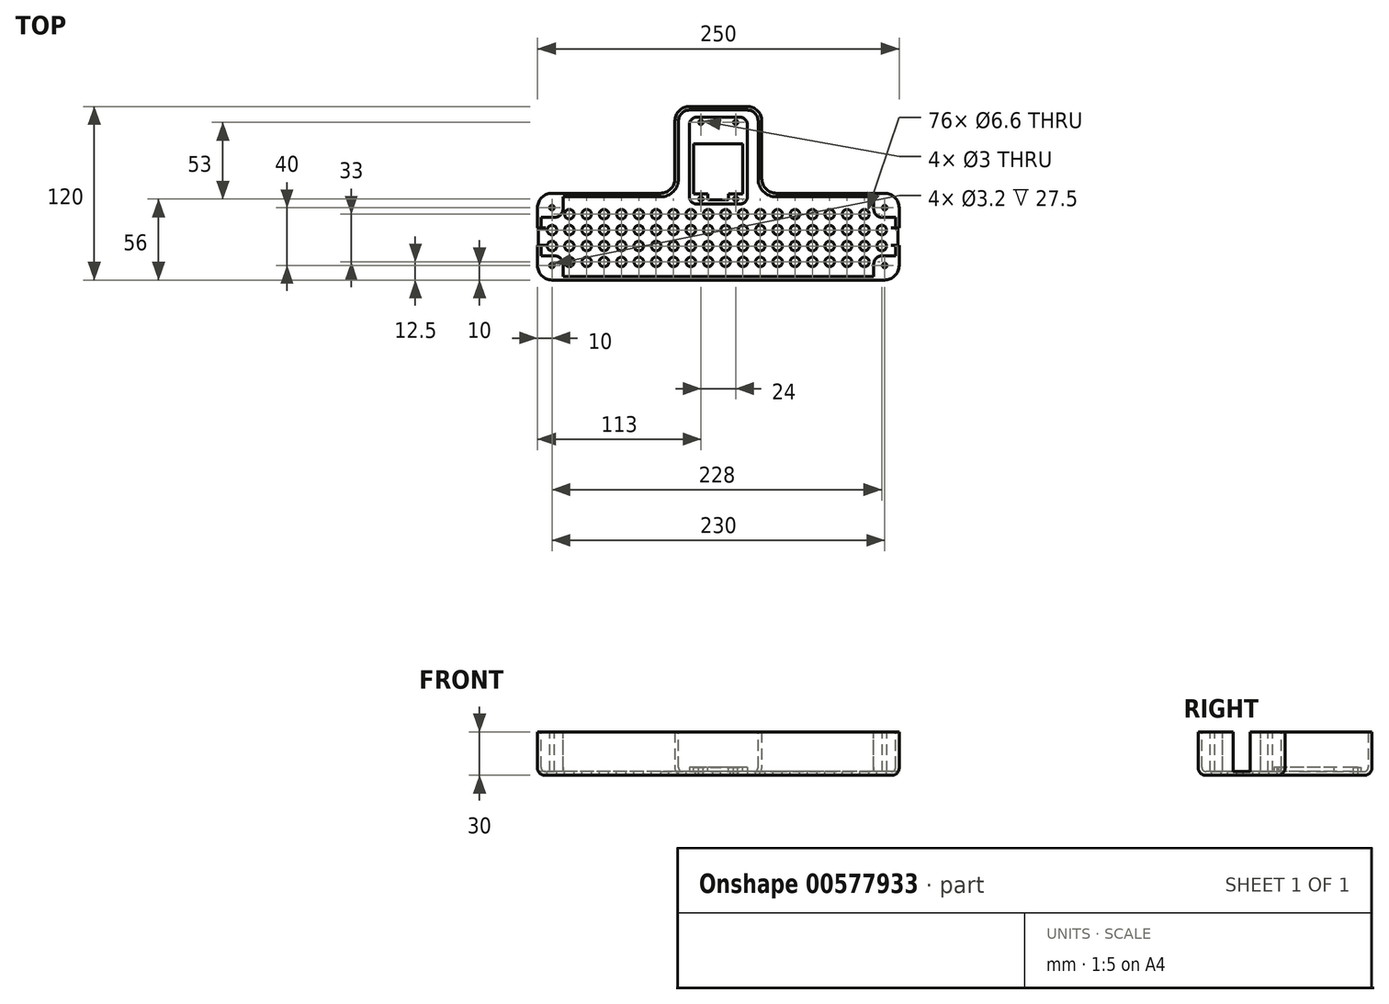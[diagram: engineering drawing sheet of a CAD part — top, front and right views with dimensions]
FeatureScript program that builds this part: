
annotation { "Feature Type Name" : "Feature", "Feature Type Description" : "" }
export const myFeature = defineFeature(function(context is Context, id is Id, definition is map)
    precondition{}
    {
        {
            var Q0;
            Q0=qCreatedBy(makeId("Top.planeOp"),FACE);
            var sketch = newSketch(context, id + "F0", { "sketchPlane" : qUnion([Q0])});
            skLineSegment(sketch, "E0.top", {"start": v(125, -30) * mm, "end": v(-125, -30) * mm});
            skLineSegment(sketch, "E0.left", {"start": v(125, 30) * mm, "end": v(125, -30) * mm});
            skLineSegment(sketch, "E0.right", {"start": v(-125, 30) * mm, "end": v(-125, -30) * mm});
            skPoint(sketch, "E0.middle", {"position": v(0, 0) * mm});
            skLineSegment(sketch, "E1.top", {"start": v(30, 90) * mm, "end": v(-30, 90) * mm});
            skLineSegment(sketch, "E1.left", {"start": v(30, 30) * mm, "end": v(30, 90) * mm});
            skLineSegment(sketch, "E1.right", {"start": v(-30, 30) * mm, "end": v(-30, 90) * mm});
            skLineSegment(sketch, "E2.trimOffspring", {"start": v(-30, 30) * mm, "end": v(-125, 30) * mm});
            skLineSegment(sketch, "E3", {"start": v(30, 30) * mm, "end": v(125, 30) * mm});
            skSolve(sketch);
        }
        {
            var Q0;
            Q0 = qSketchRegion(id + "F0", true);
            extrude(context, id + "F1", {"entities" : qUnion([Q0]), "depth" : 30 * mm, "offsetDistance" : 25 * mm});
        }
        {
            var Q0;
            Q0=makeQuery(id+"F1.opExtrude","SWEPT_EDGE",EDGE,{"disambiguationData":[OSD([sQuery(id+"F0.wireOp",EDGE,"E1.left"),sQuery(id+"F0.wireOp",EDGE,"E3")])]});
            var Q1;
            Q1=makeQuery(id+"F1.opExtrude","SWEPT_EDGE",EDGE,{"disambiguationData":[OSD([sQuery(id+"F0.wireOp",EDGE,"E1.right"),sQuery(id+"F0.wireOp",EDGE,"E2.trimOffspring")])]});
            var Q2;
            Q2=makeQuery(id+"F1.opExtrude","SWEPT_EDGE",EDGE,{"disambiguationData":[OSD([sQuery(id+"F0.wireOp",EDGE,"E1.top"),sQuery(id+"F0.wireOp",EDGE,"E1.right")])]});
            var Q3;
            Q3=makeQuery(id+"F1.opExtrude","SWEPT_EDGE",EDGE,{"disambiguationData":[OSD([sQuery(id+"F0.wireOp",EDGE,"E1.top"),sQuery(id+"F0.wireOp",EDGE,"E1.left")])]});
            var Q4;
            Q4=makeQuery(id+"F1.opExtrude","SWEPT_EDGE",EDGE,{"disambiguationData":[OSD([sQuery(id+"F0.wireOp",EDGE,"E0.left"),sQuery(id+"F0.wireOp",EDGE,"E3")])]});
            var Q5;
            Q5=makeQuery(id+"F1.opExtrude","SWEPT_EDGE",EDGE,{"disambiguationData":[OSD([sQuery(id+"F0.wireOp",EDGE,"E0.top"),sQuery(id+"F0.wireOp",EDGE,"E0.left")])]});
            var Q6;
            Q6=makeQuery(id+"F1.opExtrude","SWEPT_EDGE",EDGE,{"disambiguationData":[OSD([sQuery(id+"F0.wireOp",EDGE,"E0.top"),sQuery(id+"F0.wireOp",EDGE,"E0.right")])]});
            var Q7;
            Q7=makeQuery(id+"F1.opExtrude","SWEPT_EDGE",EDGE,{"disambiguationData":[OSD([sQuery(id+"F0.wireOp",EDGE,"E0.right"),sQuery(id+"F0.wireOp",EDGE,"E2.trimOffspring")])]});
            fillet(context, id + "F2", {"entities" : qUnion([Q0, Q1, Q2, Q3, Q4, Q5, Q6, Q7]), "radius" : 10 * mm, "tangentPropagation" : true, "allowEdgeOverflow" : false});
        }
        {
            var Q0;
            Q0=makeQuery(id+"F1.opExtrude","CAP_FACE",FACE,{"disambiguationData":[OSD([sQuery(id+"F0.wireOp",EDGE,"E0.top"),sQuery(id+"F0.wireOp",EDGE,"E0.left"),sQuery(id+"F0.wireOp",EDGE,"E0.right"),sQuery(id+"F0.wireOp",EDGE,"E1.top"),sQuery(id+"F0.wireOp",EDGE,"E1.left"),sQuery(id+"F0.wireOp",EDGE,"E1.right"),sQuery(id+"F0.wireOp",EDGE,"E2.trimOffspring"),sQuery(id+"F0.wireOp",EDGE,"E3")])],"isStart":false});
            shell(context, id + "F3", {"entities" : qUnion([Q0]), "thickness" : 2.5 * mm});
        }
        {
            var Q0;
            Q0=makeQuery(id+"F3.opShell","OFFSET_FACE",FACE,{"disambiguationData":[OSD([sQuery(id+"F0.wireOp",EDGE,"E0.top"),sQuery(id+"F0.wireOp",EDGE,"E0.left"),sQuery(id+"F0.wireOp",EDGE,"E0.right"),sQuery(id+"F0.wireOp",EDGE,"E1.top"),sQuery(id+"F0.wireOp",EDGE,"E1.left"),sQuery(id+"F0.wireOp",EDGE,"E1.right"),sQuery(id+"F0.wireOp",EDGE,"E2.trimOffspring"),sQuery(id+"F0.wireOp",EDGE,"E3")])]});
            var sketch = newSketch(context, id + "F4", { "sketchPlane" : qUnion([Q0])});
            skLineSegment(sketch, "E4.bottom", {"start": v(20, 82.5) * mm, "end": v(-20, 82.5) * mm});
            skLineSegment(sketch, "E4.top", {"start": v(20, 22.5) * mm, "end": v(-20, 22.5) * mm});
            skLineSegment(sketch, "E4.left", {"start": v(20, 82.5) * mm, "end": v(20, 22.5) * mm});
            skLineSegment(sketch, "E4.right", {"start": v(-20, 82.5) * mm, "end": v(-20, 22.5) * mm});
            skPoint(sketch, "E4.middle", {"position": v(0, 52.5) * mm});
            skSolve(sketch);
        }
        {
            var Q0;
            Q0 = qSketchRegion(id + "F4", true);
            extrude(context, id + "F5", {"entities" : qUnion([Q0]), "operationType" : NewBodyOperationType.ADD, "depth" : 3 * mm, "offsetDistance" : 25 * mm});
        }
        {
            var Q0;
            Q0=makeQuery(id+"F1.opExtrude","SWEPT_FACE",FACE,{"disambiguationData":[OSD([sQuery(id+"F0.wireOp",EDGE,"E0.right")])]});
            var sketch = newSketch(context, id + "F6", { "sketchPlane" : qUnion([Q0])});
            skLineSegment(sketch, "E5.bottom", {"start": v(6, 2.5) * mm, "end": v(-6, 2.5) * mm});
            skLineSegment(sketch, "E5.top", {"start": v(6, 30) * mm, "end": v(-6, 30) * mm});
            skLineSegment(sketch, "E5.left", {"start": v(6, 2.5) * mm, "end": v(6, 30) * mm});
            skLineSegment(sketch, "E5.right", {"start": v(-6, 2.5) * mm, "end": v(-6, 30) * mm});
            skLineSegment(sketch, "E6", {"start": v(-20, 22.59) * mm, "end": v(-6, 22.59) * mm, "construction": true});
            skLineSegment(sketch, "E7", {"start": v(6, 22.59) * mm, "end": v(20, 22.59) * mm, "construction": true});
            skSolve(sketch);
        }
        {
            var Q0;
            Q0 = qSketchRegion(id + "F6", true);
            extrude(context, id + "F7", {"entities" : qUnion([Q0]), "operationType" : NewBodyOperationType.REMOVE, "oppositeDirection" : true, "depth" : 313 * mm, "offsetDistance" : 25 * mm});
        }
        {
            var Q0;
            Q0=makeQuery(id+"F7.boolean.opBoolean","MERGE",FACE,{"derivedFrom":[makeQuery(id+"F3.opShell","OFFSET_FACE",FACE,{"disambiguationData":[OSD([sQuery(id+"F0.wireOp",EDGE,"E0.top"),sQuery(id+"F0.wireOp",EDGE,"E0.left"),sQuery(id+"F0.wireOp",EDGE,"E0.right"),sQuery(id+"F0.wireOp",EDGE,"E1.top"),sQuery(id+"F0.wireOp",EDGE,"E1.left"),sQuery(id+"F0.wireOp",EDGE,"E1.right"),sQuery(id+"F0.wireOp",EDGE,"E2.trimOffspring"),sQuery(id+"F0.wireOp",EDGE,"E3")])]}),makeQuery(id+"F7.opExtrude","SWEPT_FACE",FACE,{"disambiguationData":[OSD([sQuery(id+"F6.wireOp",EDGE,"E5.bottom")])]})]});
            var sketch = newSketch(context, id + "F8", { "sketchPlane" : qUnion([Q0])});
            skCircle(sketch, "E8", {"center": v(-115, 15.5) * mm, "radius": 3.3 * mm});
            skCircle(sketch, "E9", {"center": v(-115, 4.5) * mm, "radius": 3.3 * mm});
            skCircle(sketch, "E10.0.1.0", {"center": v(-115, -17.5) * mm, "radius": 3.3 * mm});
            skCircle(sketch, "E10.0.1.1", {"center": v(-115, -6.5) * mm, "radius": 3.3 * mm});
            skCircle(sketch, "E10.1.0.0", {"center": v(-103, 4.5) * mm, "radius": 3.3 * mm});
            skCircle(sketch, "E10.1.0.1", {"center": v(-103, 15.5) * mm, "radius": 3.3 * mm});
            skCircle(sketch, "E10.1.1.0", {"center": v(-103, -17.5) * mm, "radius": 3.3 * mm});
            skCircle(sketch, "E10.1.1.1", {"center": v(-103, -6.5) * mm, "radius": 3.3 * mm});
            skCircle(sketch, "E10.2.0.0", {"center": v(-91, 4.5) * mm, "radius": 3.3 * mm});
            skCircle(sketch, "E10.2.0.1", {"center": v(-91, 15.5) * mm, "radius": 3.3 * mm});
            skCircle(sketch, "E10.2.1.0", {"center": v(-91, -17.5) * mm, "radius": 3.3 * mm});
            skCircle(sketch, "E10.2.1.1", {"center": v(-91, -6.5) * mm, "radius": 3.3 * mm});
            skCircle(sketch, "E10.3.0.0", {"center": v(-79, 4.5) * mm, "radius": 3.3 * mm});
            skCircle(sketch, "E10.3.0.1", {"center": v(-79, 15.5) * mm, "radius": 3.3 * mm});
            skCircle(sketch, "E10.3.1.0", {"center": v(-79, -17.5) * mm, "radius": 3.3 * mm});
            skCircle(sketch, "E10.3.1.1", {"center": v(-79, -6.5) * mm, "radius": 3.3 * mm});
            skCircle(sketch, "E10.4.0.0", {"center": v(-67, 4.5) * mm, "radius": 3.3 * mm});
            skCircle(sketch, "E10.4.0.1", {"center": v(-67, 15.5) * mm, "radius": 3.3 * mm});
            skCircle(sketch, "E10.4.1.0", {"center": v(-67, -17.5) * mm, "radius": 3.3 * mm});
            skCircle(sketch, "E10.4.1.1", {"center": v(-67, -6.5) * mm, "radius": 3.3 * mm});
            skCircle(sketch, "E10.5.0.0", {"center": v(-55, 4.5) * mm, "radius": 3.3 * mm});
            skCircle(sketch, "E10.5.0.1", {"center": v(-55, 15.5) * mm, "radius": 3.3 * mm});
            skCircle(sketch, "E10.5.1.0", {"center": v(-55, -17.5) * mm, "radius": 3.3 * mm});
            skCircle(sketch, "E10.5.1.1", {"center": v(-55, -6.5) * mm, "radius": 3.3 * mm});
            skCircle(sketch, "E10.6.0.0", {"center": v(-43, 4.5) * mm, "radius": 3.3 * mm});
            skCircle(sketch, "E10.6.0.1", {"center": v(-43, 15.5) * mm, "radius": 3.3 * mm});
            skCircle(sketch, "E10.6.1.0", {"center": v(-43, -17.5) * mm, "radius": 3.3 * mm});
            skCircle(sketch, "E10.6.1.1", {"center": v(-43, -6.5) * mm, "radius": 3.3 * mm});
            skCircle(sketch, "E10.7.0.0", {"center": v(-31, 4.5) * mm, "radius": 3.3 * mm});
            skCircle(sketch, "E10.7.0.1", {"center": v(-31, 15.5) * mm, "radius": 3.3 * mm});
            skCircle(sketch, "E10.7.1.0", {"center": v(-31, -17.5) * mm, "radius": 3.3 * mm});
            skCircle(sketch, "E10.7.1.1", {"center": v(-31, -6.5) * mm, "radius": 3.3 * mm});
            skCircle(sketch, "E10.8.0.0", {"center": v(-19, 4.5) * mm, "radius": 3.3 * mm});
            skCircle(sketch, "E10.8.0.1", {"center": v(-19, 15.5) * mm, "radius": 3.3 * mm});
            skCircle(sketch, "E10.8.1.0", {"center": v(-19, -17.5) * mm, "radius": 3.3 * mm});
            skCircle(sketch, "E10.8.1.1", {"center": v(-19, -6.5) * mm, "radius": 3.3 * mm});
            skCircle(sketch, "E10.9.0.0", {"center": v(-7, 4.5) * mm, "radius": 3.3 * mm});
            skCircle(sketch, "E10.9.0.1", {"center": v(-7, 15.5) * mm, "radius": 3.3 * mm});
            skCircle(sketch, "E10.9.1.0", {"center": v(-7, -17.5) * mm, "radius": 3.3 * mm});
            skCircle(sketch, "E10.9.1.1", {"center": v(-7, -6.5) * mm, "radius": 3.3 * mm});
            skCircle(sketch, "E10.10.0.0", {"center": v(5, 4.5) * mm, "radius": 3.3 * mm});
            skCircle(sketch, "E10.10.0.1", {"center": v(5, 15.5) * mm, "radius": 3.3 * mm});
            skCircle(sketch, "E10.10.1.0", {"center": v(5, -17.5) * mm, "radius": 3.3 * mm});
            skCircle(sketch, "E10.10.1.1", {"center": v(5, -6.5) * mm, "radius": 3.3 * mm});
            skCircle(sketch, "E10.11.0.0", {"center": v(17, 4.5) * mm, "radius": 3.3 * mm});
            skCircle(sketch, "E10.11.0.1", {"center": v(17, 15.5) * mm, "radius": 3.3 * mm});
            skCircle(sketch, "E10.11.1.0", {"center": v(17, -17.5) * mm, "radius": 3.3 * mm});
            skCircle(sketch, "E10.11.1.1", {"center": v(17, -6.5) * mm, "radius": 3.3 * mm});
            skCircle(sketch, "E10.12.0.0", {"center": v(29, 4.5) * mm, "radius": 3.3 * mm});
            skCircle(sketch, "E10.12.0.1", {"center": v(29, 15.5) * mm, "radius": 3.3 * mm});
            skCircle(sketch, "E10.12.1.0", {"center": v(29, -17.5) * mm, "radius": 3.3 * mm});
            skCircle(sketch, "E10.12.1.1", {"center": v(29, -6.5) * mm, "radius": 3.3 * mm});
            skCircle(sketch, "E10.13.0.0", {"center": v(41, 4.5) * mm, "radius": 3.3 * mm});
            skCircle(sketch, "E10.13.0.1", {"center": v(41, 15.5) * mm, "radius": 3.3 * mm});
            skCircle(sketch, "E10.13.1.0", {"center": v(41, -17.5) * mm, "radius": 3.3 * mm});
            skCircle(sketch, "E10.13.1.1", {"center": v(41, -6.5) * mm, "radius": 3.3 * mm});
            skCircle(sketch, "E10.14.0.0", {"center": v(53, 4.5) * mm, "radius": 3.3 * mm});
            skCircle(sketch, "E10.14.0.1", {"center": v(53, 15.5) * mm, "radius": 3.3 * mm});
            skCircle(sketch, "E10.14.1.0", {"center": v(53, -17.5) * mm, "radius": 3.3 * mm});
            skCircle(sketch, "E10.14.1.1", {"center": v(53, -6.5) * mm, "radius": 3.3 * mm});
            skCircle(sketch, "E10.15.0.0", {"center": v(65, 4.5) * mm, "radius": 3.3 * mm});
            skCircle(sketch, "E10.15.0.1", {"center": v(65, 15.5) * mm, "radius": 3.3 * mm});
            skCircle(sketch, "E10.15.1.0", {"center": v(65, -17.5) * mm, "radius": 3.3 * mm});
            skCircle(sketch, "E10.15.1.1", {"center": v(65, -6.5) * mm, "radius": 3.3 * mm});
            skCircle(sketch, "E10.16.0.0", {"center": v(77, 4.5) * mm, "radius": 3.3 * mm});
            skCircle(sketch, "E10.16.0.1", {"center": v(77, 15.5) * mm, "radius": 3.3 * mm});
            skCircle(sketch, "E10.16.1.0", {"center": v(77, -17.5) * mm, "radius": 3.3 * mm});
            skCircle(sketch, "E10.16.1.1", {"center": v(77, -6.5) * mm, "radius": 3.3 * mm});
            skCircle(sketch, "E10.17.0.0", {"center": v(89, 4.5) * mm, "radius": 3.3 * mm});
            skCircle(sketch, "E10.17.0.1", {"center": v(89, 15.5) * mm, "radius": 3.3 * mm});
            skCircle(sketch, "E10.17.1.0", {"center": v(89, -17.5) * mm, "radius": 3.3 * mm});
            skCircle(sketch, "E10.17.1.1", {"center": v(89, -6.5) * mm, "radius": 3.3 * mm});
            skLineSegment(sketch, "E10.direction1", {"start": v(-115, 4.5) * mm, "end": v(-103, 4.5) * mm, "construction": true});
            skLineSegment(sketch, "E10.direction2", {"start": v(-115, 4.5) * mm, "end": v(-115, -17.5) * mm, "construction": true});
            skCircle(sketch, "E11.0.18.0", {"center": v(101, 4.5) * mm, "radius": 3.3 * mm});
            skCircle(sketch, "E11.2.18.0", {"center": v(101, 15.5) * mm, "radius": 3.3 * mm});
            skCircle(sketch, "E11.0.18.1", {"center": v(101, -17.5) * mm, "radius": 3.3 * mm});
            skCircle(sketch, "E11.2.18.1", {"center": v(101, -6.5) * mm, "radius": 3.3 * mm});
            skCircle(sketch, "E12.0.19.0", {"center": v(113, 4.5) * mm, "radius": 3.3 * mm});
            skCircle(sketch, "E12.2.19.0", {"center": v(113, 15.5) * mm, "radius": 3.3 * mm});
            skCircle(sketch, "E12.0.19.1", {"center": v(113, -17.5) * mm, "radius": 3.3 * mm});
            skCircle(sketch, "E12.2.19.1", {"center": v(113, -6.5) * mm, "radius": 3.3 * mm});
            skSolve(sketch);
        }
        {
            var Q0;
            Q0 = qSketchRegion(id + "F8", true);
            extrude(context, id + "F9", {"entities" : qUnion([Q0]), "operationType" : NewBodyOperationType.REMOVE, "oppositeDirection" : true, "depth" : 25 * mm, "offsetDistance" : 25 * mm});
        }
        {
            var Q0;
            {var subQ0=sQuery(id+"F0.wireOp",EDGE,"E3");var subQ1=sQuery(id+"F0.wireOp",EDGE,"E1.left");Q0=makeQuery(id+"F2.opFillet","BLEND_EDGE",EDGE,{"blendedFrom":[makeQuery(id+"F1.opExtrude","SWEPT_EDGE",EDGE,{"disambiguationData":[OSD([subQ1,subQ0])]}),makeQuery(id+"F1.opExtrude","CAP_FACE",FACE,{"disambiguationData":[OSD([sQuery(id+"F0.wireOp",EDGE,"E0.top"),sQuery(id+"F0.wireOp",EDGE,"E0.left"),sQuery(id+"F0.wireOp",EDGE,"E0.right"),sQuery(id+"F0.wireOp",EDGE,"E1.top"),subQ1,sQuery(id+"F0.wireOp",EDGE,"E1.right"),sQuery(id+"F0.wireOp",EDGE,"E2.trimOffspring"),subQ0])],"isStart":true})],"blendedInto":[makeQuery(id+"F1.opExtrude","CAP_FACE",FACE,{"disambiguationData":[OSD([sQuery(id+"F0.wireOp",EDGE,"E0.top"),sQuery(id+"F0.wireOp",EDGE,"E0.left"),sQuery(id+"F0.wireOp",EDGE,"E0.right"),sQuery(id+"F0.wireOp",EDGE,"E1.top"),subQ1,sQuery(id+"F0.wireOp",EDGE,"E1.right"),sQuery(id+"F0.wireOp",EDGE,"E2.trimOffspring"),subQ0])],"isStart":true})]});}
            fillet(context, id + "F10", {"entities" : qUnion([Q0]), "radius" : 5 * mm, "tangentPropagation" : true, "allowEdgeOverflow" : false});
        }
        {
            var Q0;
            {var subQ0=sQuery(id+"F0.wireOp",EDGE,"E2.trimOffspring");Q0=makeQuery(id+"F3.opShell","OFFSET_EDGE",EDGE,{"disambiguationData":[OSD([subQ0]),TDD([makeQuery(id+"F1.opExtrude","CAP_EDGE",EDGE,{"disambiguationData":[OSD([subQ0])],"isStart":true})])]});}
            var Q1;
            {var subQ0=sQuery(id+"F0.wireOp",EDGE,"E0.top");Q1=makeQuery(id+"F3.opShell","OFFSET_EDGE",EDGE,{"disambiguationData":[OSD([subQ0]),TDD([makeQuery(id+"F1.opExtrude","CAP_EDGE",EDGE,{"disambiguationData":[OSD([subQ0])],"isStart":true})])]});}
            fillet(context, id + "F11", {"entities" : qUnion([Q0, Q1]), "radius" : 3 * mm, "tangentPropagation" : true, "allowEdgeOverflow" : false});
        }
        {
            var Q0;
            Q0=makeQuery(id+"F5.opExtrude","CAP_FACE",FACE,{"disambiguationData":[OSD([sQuery(id+"F4.wireOp",EDGE,"E4.bottom"),sQuery(id+"F4.wireOp",EDGE,"E4.top"),sQuery(id+"F4.wireOp",EDGE,"E4.left"),sQuery(id+"F4.wireOp",EDGE,"E4.right")])],"isStart":false});
            var sketch = newSketch(context, id + "F12", { "sketchPlane" : qUnion([Q0])});
            skLineSegment(sketch, "E13.0.0", {"start": v(-20, 22.5) * mm, "end": v(20, 22.5) * mm, "construction": true});
            skLineSegment(sketch, "E13.0.1", {"start": v(20, 22.5) * mm, "end": v(20, 82.5) * mm, "construction": true});
            skLineSegment(sketch, "E13.0.2", {"start": v(20, 82.5) * mm, "end": v(-20, 82.5) * mm, "construction": true});
            skLineSegment(sketch, "E13.0.3", {"start": v(-20, 82.5) * mm, "end": v(-20, 22.5) * mm, "construction": true});
            skLineSegment(sketch, "E14", {"start": v(0, 82.5) * mm, "end": v(0, 22.5) * mm, "construction": true});
            skLineSegment(sketch, "E15.bottom", {"start": v(12, 79) * mm, "end": v(-12, 79) * mm, "construction": true});
            skLineSegment(sketch, "E15.top", {"start": v(12, 26) * mm, "end": v(-12, 26) * mm, "construction": true});
            skLineSegment(sketch, "E15.left", {"start": v(12, 79) * mm, "end": v(12, 26) * mm, "construction": true});
            skLineSegment(sketch, "E15.right", {"start": v(-12, 79) * mm, "end": v(-12, 26) * mm, "construction": true});
            skPoint(sketch, "E15.middle", {"position": v(0, 52.5) * mm});
            skCircle(sketch, "E16", {"center": v(-12, 79) * mm, "radius": 1.5 * mm});
            skCircle(sketch, "E17", {"center": v(12, 79) * mm, "radius": 1.5 * mm});
            skCircle(sketch, "E18", {"center": v(-12, 26) * mm, "radius": 1.5 * mm});
            skCircle(sketch, "E19", {"center": v(12, 26) * mm, "radius": 1.5 * mm});
            skSolve(sketch);
        }
        {
            var Q0;
            Q0 = qSketchRegion(id + "F12", true);
            extrude(context, id + "F13", {"entities" : qUnion([Q0]), "operationType" : NewBodyOperationType.REMOVE, "oppositeDirection" : true, "depth" : 25 * mm, "offsetDistance" : 25 * mm});
        }
        {
            var Q0;
            Q0=makeQuery(id+"F5.opExtrude","CAP_FACE",FACE,{"disambiguationData":[OSD([sQuery(id+"F4.wireOp",EDGE,"E4.bottom"),sQuery(id+"F4.wireOp",EDGE,"E4.top"),sQuery(id+"F4.wireOp",EDGE,"E4.left"),sQuery(id+"F4.wireOp",EDGE,"E4.right")])],"isStart":false});
            var sketch = newSketch(context, id + "F14", { "sketchPlane" : qUnion([Q0])});
            skLineSegment(sketch, "E20.0.0", {"start": v(-20, 22.5) * mm, "end": v(20, 22.5) * mm, "construction": true});
            skLineSegment(sketch, "E20.0.1", {"start": v(20, 22.5) * mm, "end": v(20, 82.5) * mm, "construction": true});
            skLineSegment(sketch, "E20.0.2", {"start": v(20, 82.5) * mm, "end": v(-20, 82.5) * mm, "construction": true});
            skLineSegment(sketch, "E20.0.3", {"start": v(-20, 82.5) * mm, "end": v(-20, 22.5) * mm, "construction": true});
            skCircle(sketch, "E21.0", {"center": v(-12, 79) * mm, "radius": 1.5 * mm, "construction": true});
            skCircle(sketch, "E22.0", {"center": v(12, 79) * mm, "radius": 1.5 * mm, "construction": true});
            skCircle(sketch, "E23.0", {"center": v(12, 26) * mm, "radius": 1.5 * mm, "construction": true});
            skCircle(sketch, "E24.0", {"center": v(-12, 26) * mm, "radius": 1.5 * mm, "construction": true});
            skLineSegment(sketch, "E25.bottom", {"start": v(-17, 64.1) * mm, "end": v(17, 64.1) * mm});
            skLineSegment(sketch, "E25.top", {"start": v(-17, 29.5) * mm, "end": v(-7.15, 29.5) * mm});
            skLineSegment(sketch, "E25.left", {"start": v(-17, 64.1) * mm, "end": v(-17, 29.5) * mm});
            skLineSegment(sketch, "E25.right", {"start": v(17, 64.1) * mm, "end": v(17, 29.5) * mm});
            skLineSegment(sketch, "E26.bottom", {"start": v(7.15, 25.5) * mm, "end": v(-7.15, 25.5) * mm});
            skLineSegment(sketch, "E26.left", {"start": v(7.15, 25.5) * mm, "end": v(7.15, 29.5) * mm});
            skLineSegment(sketch, "E26.right", {"start": v(-7.15, 25.5) * mm, "end": v(-7.15, 29.5) * mm});
            skLineSegment(sketch, "E27.trimOffspring", {"start": v(7.15, 29.5) * mm, "end": v(17, 29.5) * mm});
            skSolve(sketch);
        }
        {
            var Q0;
            Q0=makeQuery(id+"F14.imprint","IMPRINT",FACE,{"disambiguationData":[TD([[makeQuery(id+"F14.imprint","IMPRINT",EDGE,{"derivedFrom":sQuery(id+"F14.wireOp",EDGE,"E25.bottom")}),-1.0]])]});
            extrude(context, id + "F15", {"entities" : qUnion([Q0]), "operationType" : NewBodyOperationType.REMOVE, "oppositeDirection" : true, "depth" : 3 * mm, "offsetDistance" : 25 * mm});
        }
        {
            var Q0;
            Q0=makeQuery(id+"F5.opExtrude","SWEPT_EDGE",EDGE,{"disambiguationData":[OSD([sQuery(id+"F4.wireOp",EDGE,"E4.top"),sQuery(id+"F4.wireOp",EDGE,"E4.right")])]});
            var Q1;
            Q1=makeQuery(id+"F5.opExtrude","SWEPT_EDGE",EDGE,{"disambiguationData":[OSD([sQuery(id+"F4.wireOp",EDGE,"E4.top"),sQuery(id+"F4.wireOp",EDGE,"E4.left")])]});
            var Q2;
            Q2=makeQuery(id+"F5.opExtrude","SWEPT_EDGE",EDGE,{"disambiguationData":[OSD([sQuery(id+"F4.wireOp",EDGE,"E4.bottom"),sQuery(id+"F4.wireOp",EDGE,"E4.right")])]});
            var Q3;
            Q3=makeQuery(id+"F5.opExtrude","SWEPT_EDGE",EDGE,{"disambiguationData":[OSD([sQuery(id+"F4.wireOp",EDGE,"E4.bottom"),sQuery(id+"F4.wireOp",EDGE,"E4.left")])]});
            fillet(context, id + "F16", {"entities" : qUnion([Q0, Q1, Q2, Q3]), "radius" : 5 * mm, "tangentPropagation" : true, "allowEdgeOverflow" : false});
        }
        {
            var Q0;
            Q0=makeQuery(id+"F7.boolean.opBoolean","MERGE",FACE,{"derivedFrom":[makeQuery(id+"F3.opShell","OFFSET_FACE",FACE,{"disambiguationData":[OSD([sQuery(id+"F0.wireOp",EDGE,"E0.top"),sQuery(id+"F0.wireOp",EDGE,"E0.left"),sQuery(id+"F0.wireOp",EDGE,"E0.right"),sQuery(id+"F0.wireOp",EDGE,"E1.top"),sQuery(id+"F0.wireOp",EDGE,"E1.left"),sQuery(id+"F0.wireOp",EDGE,"E1.right"),sQuery(id+"F0.wireOp",EDGE,"E2.trimOffspring"),sQuery(id+"F0.wireOp",EDGE,"E3")])]}),makeQuery(id+"F7.opExtrude","SWEPT_FACE",FACE,{"disambiguationData":[OSD([sQuery(id+"F6.wireOp",EDGE,"E5.bottom")])]})]});
            var sketch = newSketch(context, id + "F17", { "sketchPlane" : qUnion([Q0])});
            skCircle(sketch, "E28.0", {"center": v(-115, 15.5) * mm, "radius": 3.3 * mm});
            skCircle(sketch, "E29.0", {"center": v(113, 15.5) * mm, "radius": 3.3 * mm});
            skCircle(sketch, "E30.0", {"center": v(113, -17.5) * mm, "radius": 3.3 * mm});
            skCircle(sketch, "E31.0", {"center": v(-115, -17.5) * mm, "radius": 3.3 * mm});
            skSolve(sketch);
        }
        {
            var Q0;
            Q0 = qSketchRegion(id + "F17", true);
            var Q1;
            Q1=makeQuery(id+"F1.opExtrude","CAP_FACE",FACE,{"disambiguationData":[OSD([sQuery(id+"F0.wireOp",EDGE,"E0.top"),sQuery(id+"F0.wireOp",EDGE,"E0.left"),sQuery(id+"F0.wireOp",EDGE,"E0.right"),sQuery(id+"F0.wireOp",EDGE,"E1.top"),sQuery(id+"F0.wireOp",EDGE,"E1.left"),sQuery(id+"F0.wireOp",EDGE,"E1.right"),sQuery(id+"F0.wireOp",EDGE,"E2.trimOffspring"),sQuery(id+"F0.wireOp",EDGE,"E3")])],"isStart":true});
            extrude(context, id + "F18", {"entities" : qUnion([Q0]), "operationType" : NewBodyOperationType.ADD, "endBound" : BoundingType.UP_TO_SURFACE, "oppositeDirection" : true, "depth" : 25 * mm, "endBoundEntityFace" : qUnion([Q1]), "offsetDistance" : 25 * mm});
        }
        {
            var Q0;
            {var subQ0=sQuery(id+"F0.wireOp",EDGE,"E2.trimOffspring");var subQ1=sQuery(id+"F0.wireOp",EDGE,"E1.right");var subQ2=sQuery(id+"F0.wireOp",EDGE,"E3");var subQ3=sQuery(id+"F0.wireOp",EDGE,"E1.left");var subQ4=sQuery(id+"F0.wireOp",EDGE,"E1.top");var subQ5=sQuery(id+"F0.wireOp",EDGE,"E0.right");var subQ6=sQuery(id+"F0.wireOp",EDGE,"E0.left");Q0=makeQuery(id+"F7.boolean.opBoolean","SPLIT",FACE,{"disambiguationData":[TD([makeQuery(id+"F1.opExtrude","SWEPT_FACE",FACE,{"disambiguationData":[OSD([subQ4])]})])],"derivedFrom":makeQuery(id+"F1.opExtrude","CAP_FACE",FACE,{"disambiguationData":[OSD([sQuery(id+"F0.wireOp",EDGE,"E0.top"),subQ6,subQ5,subQ4,subQ3,subQ1,subQ0,subQ2])],"isStart":false})});}
            var sketch = newSketch(context, id + "F19", { "sketchPlane" : qUnion([Q0])});
            skArc(sketch, "E32.0", {"start": v(125, 20) * mm, "mid": v(122.07, 27.07) * mm, "end": v(115, 30) * mm, "construction": true});
            skCircle(sketch, "E32.1", {"center": v(5, -6.5) * mm, "radius": 3.3 * mm, "construction": true});
            skArc(sketch, "E32.2", {"start": v(-30, 40) * mm, "mid": v(-32.93, 32.93) * mm, "end": v(-40, 30) * mm, "construction": true});
            skArc(sketch, "E32.3", {"start": v(-125, -20) * mm, "mid": v(-122.07, -27.07) * mm, "end": v(-115, -30) * mm, "construction": true});
            skArc(sketch, "E32.4", {"start": v(115, -30) * mm, "mid": v(122.07, -27.07) * mm, "end": v(125, -20) * mm, "construction": true});
            skArc(sketch, "E32.5", {"start": v(-115, 30) * mm, "mid": v(-122.07, 27.07) * mm, "end": v(-125, 20) * mm, "construction": true});
            skLineSegment(sketch, "E32.6", {"start": v(-40, 30) * mm, "end": v(-115, 30) * mm, "construction": true});
            skLineSegment(sketch, "E32.7", {"start": v(40, 30) * mm, "end": v(115, 30) * mm, "construction": true});
            skLineSegment(sketch, "E32.8", {"start": v(115, -30) * mm, "end": v(-115, -30) * mm, "construction": true});
            skArc(sketch, "E32.9", {"start": v(-20, 90) * mm, "mid": v(-27.07, 87.07) * mm, "end": v(-30, 80) * mm, "construction": true});
            skCircle(sketch, "E32.10", {"center": v(-43, -17.5) * mm, "radius": 3.3 * mm, "construction": true});
            skLineSegment(sketch, "E32.11", {"start": v(20, 90) * mm, "end": v(-20, 90) * mm, "construction": true});
            skArc(sketch, "E32.12", {"start": v(40, 30) * mm, "mid": v(32.93, 32.93) * mm, "end": v(30, 40) * mm, "construction": true});
            skLineSegment(sketch, "E32.13", {"start": v(30, 40) * mm, "end": v(30, 80) * mm, "construction": true});
            skCircle(sketch, "E32.14", {"center": v(-55, 15.5) * mm, "radius": 3.3 * mm, "construction": true});
            skLineSegment(sketch, "E32.15", {"start": v(-30, 40) * mm, "end": v(-30, 80) * mm, "construction": true});
            skArc(sketch, "E32.16", {"start": v(-115, 27.5) * mm, "mid": v(-120.3, 25.3) * mm, "end": v(-122.5, 20) * mm, "construction": true});
            skArc(sketch, "E32.17", {"start": v(115, -27.5) * mm, "mid": v(120.3, -25.3) * mm, "end": v(122.5, -20) * mm, "construction": true});
            skArc(sketch, "E32.18", {"start": v(-27.5, 40) * mm, "mid": v(-31.16, 31.16) * mm, "end": v(-40, 27.5) * mm, "construction": true});
            skLineSegment(sketch, "E32.19", {"start": v(-40, 27.5) * mm, "end": v(-115, 27.5) * mm, "construction": true});
            skLineSegment(sketch, "E32.20", {"start": v(40, 27.5) * mm, "end": v(115, 27.5) * mm, "construction": true});
            skCircle(sketch, "E32.21", {"center": v(5, -17.5) * mm, "radius": 3.3 * mm, "construction": true});
            skArc(sketch, "E32.22", {"start": v(27.5, 80) * mm, "mid": v(25.3, 85.3) * mm, "end": v(20, 87.5) * mm, "construction": true});
            skLineSegment(sketch, "E32.23", {"start": v(115, -27.5) * mm, "end": v(-115, -27.5) * mm, "construction": true});
            skCircle(sketch, "E32.24", {"center": v(-103, -6.5) * mm, "radius": 3.3 * mm, "construction": true});
            skLineSegment(sketch, "E32.25", {"start": v(20, 87.5) * mm, "end": v(-20, 87.5) * mm, "construction": true});
            skArc(sketch, "E32.26", {"start": v(40, 27.5) * mm, "mid": v(31.16, 31.16) * mm, "end": v(27.5, 40) * mm, "construction": true});
            skLineSegment(sketch, "E32.27", {"start": v(27.5, 40) * mm, "end": v(27.5, 80) * mm, "construction": true});
            skLineSegment(sketch, "E32.28", {"start": v(-27.5, 40) * mm, "end": v(-27.5, 80) * mm, "construction": true});
            skCircle(sketch, "E32.29", {"center": v(89, 4.5) * mm, "radius": 3.3 * mm, "construction": true});
            skCircle(sketch, "E32.30", {"center": v(53, 15.5) * mm, "radius": 3.3 * mm, "construction": true});
            skCircle(sketch, "E32.31", {"center": v(-91, -17.5) * mm, "radius": 3.3 * mm, "construction": true});
            skCircle(sketch, "E32.32", {"center": v(53, -6.5) * mm, "radius": 3.3 * mm, "construction": true});
            skLineSegment(sketch, "E32.33", {"start": v(-17, 64.1) * mm, "end": v(17, 64.1) * mm, "construction": true});
            skCircle(sketch, "E32.34", {"center": v(101, 15.5) * mm, "radius": 3.3 * mm, "construction": true});
            skCircle(sketch, "E32.35", {"center": v(-55, 4.5) * mm, "radius": 3.3 * mm, "construction": true});
            skCircle(sketch, "E32.36", {"center": v(-55, -17.5) * mm, "radius": 3.3 * mm, "construction": true});
            skCircle(sketch, "E32.37", {"center": v(101, -17.5) * mm, "radius": 3.3 * mm, "construction": true});
            skCircle(sketch, "E32.38", {"center": v(-7, -17.5) * mm, "radius": 3.3 * mm, "construction": true});
            skCircle(sketch, "E32.39", {"center": v(89, -6.5) * mm, "radius": 3.3 * mm, "construction": true});
            skCircle(sketch, "E32.40", {"center": v(41, -6.5) * mm, "radius": 3.3 * mm, "construction": true});
            skCircle(sketch, "E32.41", {"center": v(89, -17.5) * mm, "radius": 3.3 * mm, "construction": true});
            skCircle(sketch, "E32.42", {"center": v(53, 4.5) * mm, "radius": 3.3 * mm, "construction": true});
            skCircle(sketch, "E32.43", {"center": v(-7, -6.5) * mm, "radius": 3.3 * mm, "construction": true});
            skCircle(sketch, "E32.44", {"center": v(41, -17.5) * mm, "radius": 3.3 * mm, "construction": true});
            skCircle(sketch, "E32.45", {"center": v(113, 4.5) * mm, "radius": 3.3 * mm, "construction": true});
            skLineSegment(sketch, "E32.46", {"start": v(7.15, 25.5) * mm, "end": v(-7.15, 25.5) * mm, "construction": true});
            skCircle(sketch, "E32.47", {"center": v(101, -6.5) * mm, "radius": 3.3 * mm, "construction": true});
            skCircle(sketch, "E32.48", {"center": v(-7, 15.5) * mm, "radius": 3.3 * mm, "construction": true});
            skLineSegment(sketch, "E32.49", {"start": v(40, 27.5) * mm, "end": v(40, 24.5) * mm, "construction": true});
            skCircle(sketch, "E32.50", {"center": v(-43, -6.5) * mm, "radius": 3.3 * mm, "construction": true});
            skCircle(sketch, "E32.51", {"center": v(41, 15.5) * mm, "radius": 3.3 * mm, "construction": true});
            skCircle(sketch, "E32.52", {"center": v(-55, -6.5) * mm, "radius": 3.3 * mm, "construction": true});
            skLineSegment(sketch, "E32.53", {"start": v(125, 20) * mm, "end": v(125, 6) * mm, "construction": true});
            skCircle(sketch, "E32.54", {"center": v(53, -17.5) * mm, "radius": 3.3 * mm, "construction": true});
            skCircle(sketch, "E32.55", {"center": v(17, 4.5) * mm, "radius": 3.3 * mm, "construction": true});
            skCircle(sketch, "E32.56", {"center": v(-43, 15.5) * mm, "radius": 3.3 * mm, "construction": true});
            skCircle(sketch, "E32.57", {"center": v(5, 15.5) * mm, "radius": 3.3 * mm, "construction": true});
            skCircle(sketch, "E32.58", {"center": v(89, 15.5) * mm, "radius": 3.3 * mm, "construction": true});
            skCircle(sketch, "E32.59", {"center": v(29, -6.5) * mm, "radius": 3.3 * mm, "construction": true});
            skCircle(sketch, "E32.60", {"center": v(-19, -6.5) * mm, "radius": 3.3 * mm, "construction": true});
            skCircle(sketch, "E32.61", {"center": v(77, -17.5) * mm, "radius": 3.3 * mm, "construction": true});
            skCircle(sketch, "E32.62", {"center": v(29, -17.5) * mm, "radius": 3.3 * mm, "construction": true});
            skLineSegment(sketch, "E32.63", {"start": v(-122.5, 20) * mm, "end": v(-122.5, 6) * mm, "construction": true});
            skCircle(sketch, "E32.64", {"center": v(-19, -17.5) * mm, "radius": 3.3 * mm, "construction": true});
            skCircle(sketch, "E32.65", {"center": v(-67, -17.5) * mm, "radius": 3.3 * mm, "construction": true});
            skCircle(sketch, "E32.66", {"center": v(77, 15.5) * mm, "radius": 3.3 * mm, "construction": true});
            skCircle(sketch, "E32.67", {"center": v(-19, 15.5) * mm, "radius": 3.3 * mm, "construction": true});
            skCircle(sketch, "E32.68", {"center": v(29, 15.5) * mm, "radius": 3.3 * mm, "construction": true});
            skCircle(sketch, "E32.69", {"center": v(-67, 15.5) * mm, "radius": 3.3 * mm, "construction": true});
            skCircle(sketch, "E32.70", {"center": v(77, 4.5) * mm, "radius": 3.3 * mm, "construction": true});
            skCircle(sketch, "E32.71", {"center": v(-19, 4.5) * mm, "radius": 3.3 * mm, "construction": true});
            skCircle(sketch, "E32.72", {"center": v(-79, 4.5) * mm, "radius": 3.3 * mm, "construction": true});
            skCircle(sketch, "E32.73", {"center": v(-79, 15.5) * mm, "radius": 3.3 * mm, "construction": true});
            skLineSegment(sketch, "E32.74", {"start": v(125, -6) * mm, "end": v(125, -20) * mm, "construction": true});
            skCircle(sketch, "E32.75", {"center": v(113, -6.5) * mm, "radius": 3.3 * mm, "construction": true});
            skCircle(sketch, "E32.76", {"center": v(65, -17.5) * mm, "radius": 3.3 * mm, "construction": true});
            skCircle(sketch, "E32.77", {"center": v(-91, 15.5) * mm, "radius": 3.3 * mm, "construction": true});
            skLineSegment(sketch, "E32.78", {"start": v(-122.5, -6) * mm, "end": v(-122.5, -20) * mm, "construction": true});
            skLineSegment(sketch, "E32.79", {"start": v(-115, 27.5) * mm, "end": v(-115, 24.5) * mm, "construction": true});
            skCircle(sketch, "E32.80", {"center": v(-91, 4.5) * mm, "radius": 3.3 * mm, "construction": true});
            skCircle(sketch, "E32.81", {"center": v(-79, -17.5) * mm, "radius": 3.3 * mm, "construction": true});
            skCircle(sketch, "E32.82", {"center": v(-91, -6.5) * mm, "radius": 3.3 * mm, "construction": true});
            skCircle(sketch, "E32.83", {"center": v(77, -6.5) * mm, "radius": 3.3 * mm, "construction": true});
            skCircle(sketch, "E32.84", {"center": v(-67, -6.5) * mm, "radius": 3.3 * mm, "construction": true});
            skCircle(sketch, "E32.85", {"center": v(17, -6.5) * mm, "radius": 3.3 * mm, "construction": true});
            skCircle(sketch, "E32.86", {"center": v(-79, -6.5) * mm, "radius": 3.3 * mm, "construction": true});
            skCircle(sketch, "E32.87", {"center": v(17, -17.5) * mm, "radius": 3.3 * mm, "construction": true});
            skCircle(sketch, "E32.88", {"center": v(-31, -17.5) * mm, "radius": 3.3 * mm, "construction": true});
            skCircle(sketch, "E32.89", {"center": v(65, 15.5) * mm, "radius": 3.3 * mm, "construction": true});
            skCircle(sketch, "E32.90", {"center": v(-31, 15.5) * mm, "radius": 3.3 * mm, "construction": true});
            skLineSegment(sketch, "E32.91", {"start": v(122.5, -6) * mm, "end": v(122.5, -20) * mm, "construction": true});
            skCircle(sketch, "E32.92", {"center": v(-115, -6.5) * mm, "radius": 3.3 * mm, "construction": true});
            skLineSegment(sketch, "E32.93", {"start": v(122.5, 20) * mm, "end": v(122.5, 6) * mm, "construction": true});
            skLineSegment(sketch, "E32.94", {"start": v(-125, -6) * mm, "end": v(-125, -20) * mm, "construction": true});
            skLineSegment(sketch, "E32.95", {"start": v(-125, 20) * mm, "end": v(-125, 6) * mm, "construction": true});
            skCircle(sketch, "E32.96", {"center": v(-103, 15.5) * mm, "radius": 3.3 * mm, "construction": true});
            skLineSegment(sketch, "E32.97", {"start": v(15, 82.5) * mm, "end": v(-15, 82.5) * mm, "construction": true});
            skLineSegment(sketch, "E32.98", {"start": v(15, 22.5) * mm, "end": v(-15, 22.5) * mm, "construction": true});
            skLineSegment(sketch, "E32.99", {"start": v(20, 77.5) * mm, "end": v(20, 27.5) * mm, "construction": true});
            skLineSegment(sketch, "E32.100", {"start": v(-20, 77.5) * mm, "end": v(-20, 27.5) * mm, "construction": true});
            skArc(sketch, "E33.0", {"start": v(122.5, 20) * mm, "mid": v(120.3, 25.3) * mm, "end": v(115, 27.5) * mm, "construction": true});
            skLineSegment(sketch, "E34", {"start": v(107.4, 27.5) * mm, "end": v(107.4, 13.3) * mm});
            skLineSegment(sketch, "E35", {"start": v(107.4, 13.3) * mm, "end": v(122.5, 13.3) * mm});
            skLineSegment(sketch, "E36", {"start": v(107.4, 27.5) * mm, "end": v(115, 27.5) * mm});
            skLineSegment(sketch, "E37", {"start": v(122.5, 20) * mm, "end": v(122.5, 13.3) * mm});
            skLineSegment(sketch, "E38.MirrorCS", {"start": v(107.4, -27.5) * mm, "end": v(107.4, -13.3) * mm});
            skLineSegment(sketch, "E39.MirrorCS", {"start": v(107.4, -13.3) * mm, "end": v(122.5, -13.3) * mm});
            skLineSegment(sketch, "E40.MirrorCS", {"start": v(122.5, -20) * mm, "end": v(122.5, -13.3) * mm});
            skLineSegment(sketch, "E41.MirrorCS", {"start": v(107.4, -27.5) * mm, "end": v(115, -27.5) * mm});
            skArc(sketch, "E42.MirrorCS", {"start": v(122.5, -20) * mm, "mid": v(120.3, -25.3) * mm, "end": v(115, -27.5) * mm, "construction": true});
            skLineSegment(sketch, "E43", {"start": v(147.05, 0) * mm, "end": v(-175.17, 0) * mm, "construction": true});
            skLineSegment(sketch, "E44", {"start": v(0, 100.69) * mm, "end": v(0, -102.58) * mm, "construction": true});
            skPoint(sketch, "E44.startSnap0", {"position": v(0, 90) * mm});
            skPoint(sketch, "E44.endSnap0", {"position": v(0, -27.5) * mm});
            skLineSegment(sketch, "E45.MirrorCS", {"start": v(-107.4, -27.5) * mm, "end": v(-115, -27.5) * mm});
            skLineSegment(sketch, "E46.MirrorCS", {"start": v(-107.4, -13.3) * mm, "end": v(-122.5, -13.3) * mm});
            skLineSegment(sketch, "E47.MirrorCS", {"start": v(-107.4, -27.5) * mm, "end": v(-107.4, -13.3) * mm});
            skArc(sketch, "E48.MirrorCS", {"start": v(-122.5, -20) * mm, "mid": v(-120.3, -25.3) * mm, "end": v(-115, -27.5) * mm, "construction": true});
            skLineSegment(sketch, "E49.MirrorCS", {"start": v(-122.5, -20) * mm, "end": v(-122.5, -13.3) * mm});
            skArc(sketch, "E50.MirrorCS", {"start": v(-115, -27.5) * mm, "mid": v(-120.3, -25.3) * mm, "end": v(-122.5, -20) * mm, "construction": true});
            skLineSegment(sketch, "E51.MirrorCS", {"start": v(-107.4, 27.5) * mm, "end": v(-107.4, 13.3) * mm});
            skLineSegment(sketch, "E52.MirrorCS", {"start": v(-107.4, 13.3) * mm, "end": v(-122.5, 13.3) * mm});
            skLineSegment(sketch, "E53.MirrorCS", {"start": v(-107.4, 27.5) * mm, "end": v(-115, 27.5) * mm});
            skLineSegment(sketch, "E54.MirrorCS", {"start": v(-122.5, 20) * mm, "end": v(-122.5, 13.3) * mm});
            skArc(sketch, "E55.MirrorCS", {"start": v(-122.5, 20) * mm, "mid": v(-120.3, 25.3) * mm, "end": v(-115, 27.5) * mm, "construction": true});
            skLineSegment(sketch, "E56.0.0", {"start": v(125, -20) * mm, "end": v(125, -6) * mm});
            skLineSegment(sketch, "E56.0.1", {"start": v(125, -6) * mm, "end": v(122.5, -6) * mm});
            skLineSegment(sketch, "E56.0.2", {"start": v(122.5, -6) * mm, "end": v(122.5, -20) * mm});
            skArc(sketch, "E56.0.3", {"start": v(122.5, -20) * mm, "mid": v(120.3, -25.3) * mm, "end": v(115, -27.5) * mm});
            skLineSegment(sketch, "E56.0.4", {"start": v(115, -27.5) * mm, "end": v(-115, -27.5) * mm});
            skArc(sketch, "E56.0.5", {"start": v(-115, -27.5) * mm, "mid": v(-120.3, -25.3) * mm, "end": v(-122.5, -20) * mm});
            skLineSegment(sketch, "E56.0.6", {"start": v(-122.5, -20) * mm, "end": v(-122.5, -6) * mm});
            skLineSegment(sketch, "E56.0.7", {"start": v(-122.5, -6) * mm, "end": v(-125, -6) * mm});
            skLineSegment(sketch, "E56.0.8", {"start": v(-125, -6) * mm, "end": v(-125, -20) * mm});
            skArc(sketch, "E56.0.9", {"start": v(-125, -20) * mm, "mid": v(-122.07, -27.07) * mm, "end": v(-115, -30) * mm});
            skLineSegment(sketch, "E56.0.10", {"start": v(-115, -30) * mm, "end": v(115, -30) * mm});
            skArc(sketch, "E56.0.11", {"start": v(115, -30) * mm, "mid": v(122.07, -27.07) * mm, "end": v(125, -20) * mm});
            skCircle(sketch, "E57", {"center": v(115, 20) * mm, "radius": 1.6 * mm});
            skCircle(sketch, "E58", {"center": v(115, -20) * mm, "radius": 1.6 * mm});
            skCircle(sketch, "E59", {"center": v(-115, -20) * mm, "radius": 1.6 * mm});
            skCircle(sketch, "E60", {"center": v(-115, 20) * mm, "radius": 1.6 * mm});
            skSolve(sketch);
        }
        {
            var Q0;
            Q0=makeQuery(id+"F19.imprint","IMPRINT",FACE,{"disambiguationData":[TD([[makeQuery(id+"F19.imprint","IMPRINT",EDGE,{"derivedFrom":sQuery(id+"F19.wireOp",EDGE,"E51.MirrorCS")}),-1.0]])]});
            var Q1;
            {var subQ2=sQuery(id+"F19.wireOp",EDGE,"E47.MirrorCS");Q1=makeQuery(id+"F19.imprint","IMPRINT",FACE,{"disambiguationData":[TD([[makeQuery(id+"F19.imprint","IMPRINT",EDGE,{"derivedFrom":subQ2}),1.0]])]});}
            var Q2;
            {var subQ3=sQuery(id+"F19.wireOp",EDGE,"E39.MirrorCS");Q2=makeQuery(id+"F19.imprint","IMPRINT",FACE,{"disambiguationData":[TD([[makeQuery(id+"F19.imprint","IMPRINT",EDGE,{"derivedFrom":subQ3}),-1.0]])]});}
            var Q3;
            Q3=makeQuery(id+"F19.imprint","IMPRINT",FACE,{"disambiguationData":[TD([[makeQuery(id+"F19.imprint","IMPRINT",EDGE,{"derivedFrom":sQuery(id+"F19.wireOp",EDGE,"E34")}),1.0]])]});
            var Q4;
            Q4=makeQuery(id+"F18.boolean.opBoolean","MERGE",FACE,{"derivedFrom":[makeQuery(id+"F7.boolean.opBoolean","MERGE",FACE,{"derivedFrom":[makeQuery(id+"F3.opShell","OFFSET_FACE",FACE,{"disambiguationData":[OSD([sQuery(id+"F0.wireOp",EDGE,"E0.top"),sQuery(id+"F0.wireOp",EDGE,"E0.left"),sQuery(id+"F0.wireOp",EDGE,"E0.right"),sQuery(id+"F0.wireOp",EDGE,"E1.top"),sQuery(id+"F0.wireOp",EDGE,"E1.left"),sQuery(id+"F0.wireOp",EDGE,"E1.right"),sQuery(id+"F0.wireOp",EDGE,"E2.trimOffspring"),sQuery(id+"F0.wireOp",EDGE,"E3")])]}),makeQuery(id+"F7.opExtrude","SWEPT_FACE",FACE,{"disambiguationData":[OSD([sQuery(id+"F6.wireOp",EDGE,"E5.bottom")])]})]}),makeQuery(id+"F18.opExtrude","CAP_FACE",FACE,{"disambiguationData":[OSD([sQuery(id+"F17.wireOp",EDGE,"E28.0")])],"isStart":true}),makeQuery(id+"F18.opExtrude","CAP_FACE",FACE,{"disambiguationData":[OSD([sQuery(id+"F17.wireOp",EDGE,"E29.0")])],"isStart":true}),makeQuery(id+"F18.opExtrude","CAP_FACE",FACE,{"disambiguationData":[OSD([sQuery(id+"F17.wireOp",EDGE,"E30.0")])],"isStart":true}),makeQuery(id+"F18.opExtrude","CAP_FACE",FACE,{"disambiguationData":[OSD([sQuery(id+"F17.wireOp",EDGE,"E31.0")])],"isStart":true})]});
            extrude(context, id + "F20", {"entities" : qUnion([Q0, Q1, Q2, Q3]), "operationType" : NewBodyOperationType.ADD, "endBound" : BoundingType.UP_TO_SURFACE, "oppositeDirection" : true, "depth" : 25 * mm, "endBoundEntityFace" : qUnion([Q4]), "offsetDistance" : 25 * mm});
        }
        {
            var Q0;
            Q0=makeQuery(id+"F20.opExtrude","SWEPT_EDGE",EDGE,{"disambiguationData":[OSD([sQuery(id+"F19.wireOp",EDGE,"E51.MirrorCS"),sQuery(id+"F19.wireOp",EDGE,"E52.MirrorCS")])]});
            var Q1;
            Q1=makeQuery(id+"F20.opExtrude","SWEPT_EDGE",EDGE,{"disambiguationData":[OSD([sQuery(id+"F19.wireOp",EDGE,"E34"),sQuery(id+"F19.wireOp",EDGE,"E35")])]});
            var Q2;
            Q2=makeQuery(id+"F20.opExtrude","SWEPT_EDGE",EDGE,{"disambiguationData":[OSD([sQuery(id+"F19.wireOp",EDGE,"E39.MirrorCS"),sQuery(id+"F19.wireOp",EDGE,"E38.MirrorCS")])]});
            var Q3;
            Q3=makeQuery(id+"F20.opExtrude","SWEPT_EDGE",EDGE,{"disambiguationData":[OSD([sQuery(id+"F19.wireOp",EDGE,"E47.MirrorCS"),sQuery(id+"F19.wireOp",EDGE,"E46.MirrorCS")])]});
            fillet(context, id + "F21", {"entities" : qUnion([Q0, Q1, Q2, Q3]), "radius" : 6 * mm, "tangentPropagation" : true, "allowEdgeOverflow" : false});
        }
        {
            var Q0;
            {var subQ0=sQuery(id+"F0.wireOp",EDGE,"E3");var subQ1=sQuery(id+"F0.wireOp",EDGE,"E2.trimOffspring");var subQ2=sQuery(id+"F0.wireOp",EDGE,"E1.right");var subQ3=sQuery(id+"F0.wireOp",EDGE,"E1.left");var subQ4=sQuery(id+"F0.wireOp",EDGE,"E1.top");var subQ5=sQuery(id+"F0.wireOp",EDGE,"E0.right");var subQ6=sQuery(id+"F0.wireOp",EDGE,"E0.left");var subQ7=sQuery(id+"F0.wireOp",EDGE,"E0.top");Q0=makeQuery(id+"F20.boolean.opBoolean","MERGE",FACE,{"derivedFrom":[makeQuery(id+"F7.boolean.opBoolean","SPLIT",FACE,{"disambiguationData":[TD([makeQuery(id+"F1.opExtrude","SWEPT_FACE",FACE,{"disambiguationData":[OSD([subQ4])]})])],"derivedFrom":makeQuery(id+"F1.opExtrude","CAP_FACE",FACE,{"disambiguationData":[OSD([subQ7,subQ6,subQ5,subQ4,subQ3,subQ2,subQ1,subQ0])],"isStart":false})}),makeQuery(id+"F20.opExtrude","CAP_FACE",FACE,{"disambiguationData":[OSD([subQ7,subQ6,subQ5,subQ4,subQ3,subQ2,subQ1,subQ0,sQuery(id+"F19.wireOp",EDGE,"E34"),sQuery(id+"F19.wireOp",EDGE,"E35"),sQuery(id+"F19.wireOp",EDGE,"E36"),sQuery(id+"F19.wireOp",EDGE,"E37"),sQuery(id+"F19.wireOp",EDGE,"E57")])],"isStart":true}),makeQuery(id+"F20.opExtrude","CAP_FACE",FACE,{"disambiguationData":[OSD([subQ7,subQ6,subQ5,subQ4,subQ3,subQ2,subQ1,subQ0,sQuery(id+"F19.wireOp",EDGE,"E51.MirrorCS"),sQuery(id+"F19.wireOp",EDGE,"E52.MirrorCS"),sQuery(id+"F19.wireOp",EDGE,"E53.MirrorCS"),sQuery(id+"F19.wireOp",EDGE,"E54.MirrorCS"),sQuery(id+"F19.wireOp",EDGE,"E60")])],"isStart":true})]});}
            cPlane(context, id + "F22", {"entities" : qUnion([Q0]), "cplaneType" : CPlaneType.OFFSET, "offset" : 25 * mm, "width" : 150 * mm, "height" : 150 * mm});
        }
    });
